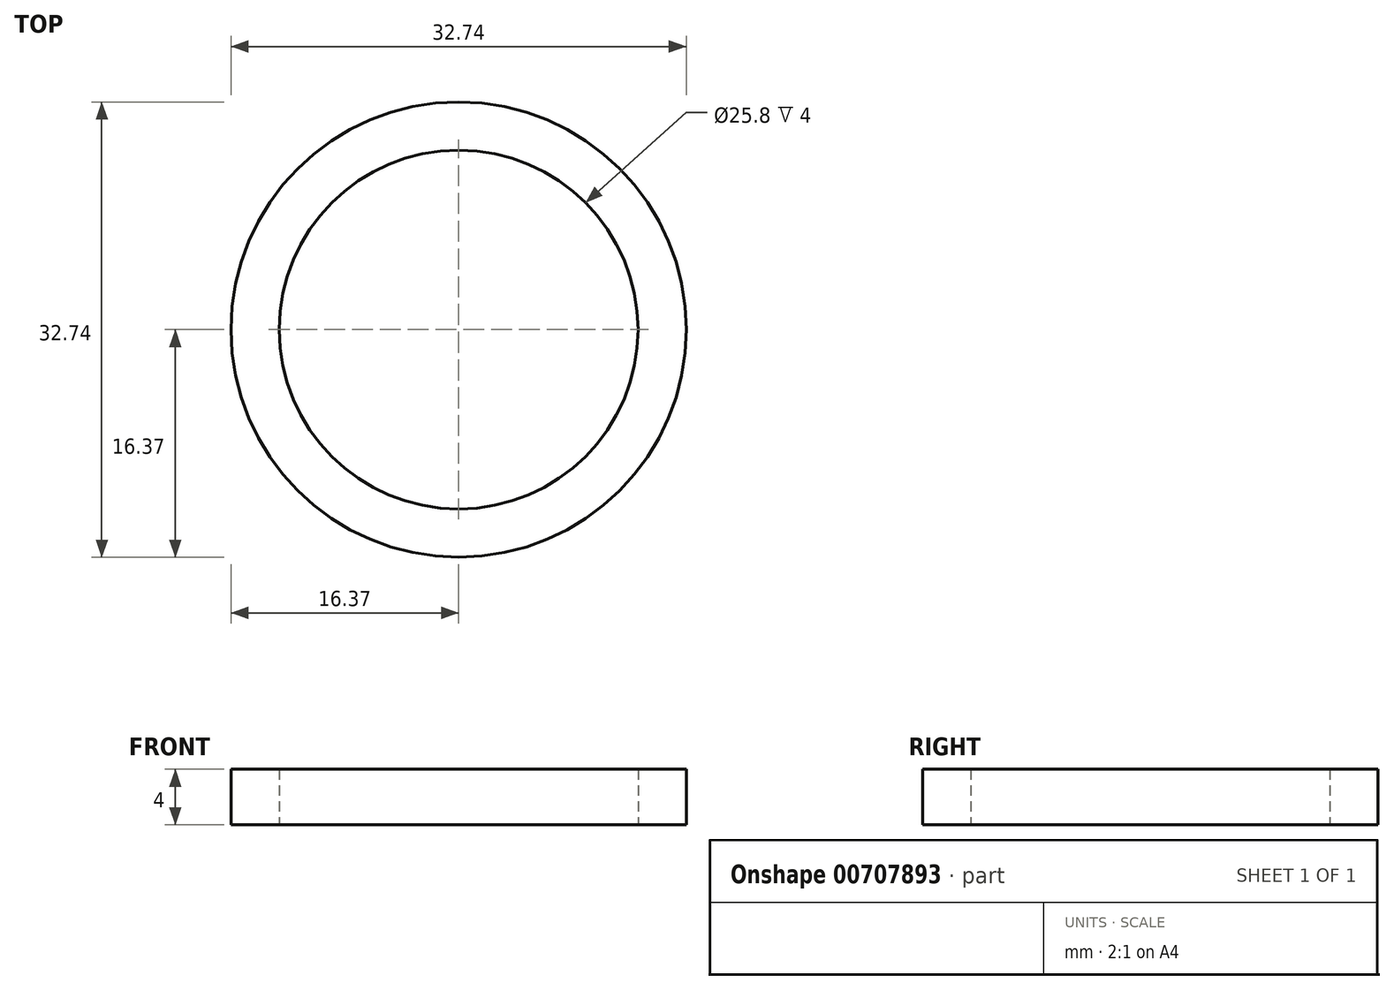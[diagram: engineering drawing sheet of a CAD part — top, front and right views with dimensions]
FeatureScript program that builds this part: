
annotation { "Feature Type Name" : "Feature", "Feature Type Description" : "" }
export const myFeature = defineFeature(function(context is Context, id is Id, definition is map)
    precondition{}
    {
        {
            var Q0;
            Q0=qCreatedBy(makeId("Top.planeOp"),FACE);
            var sketch = newSketch(context, id + "F0", { "sketchPlane" : qUnion([Q0])});
            skCircle(sketch, "E0", {"center": v(0, 0) * mm, "radius": 12.9 * mm});
            skCircle(sketch, "E1", {"center": v(0, 0) * mm, "radius": 16.37 * mm});
            skSolve(sketch);
        }
        {
            var Q0;
            Q0=makeQuery(id+"F0.imprint","IMPRINT",FACE,{"disambiguationData":[TD([[makeQuery(id+"F0.imprint","IMPRINT",EDGE,{"derivedFrom":sQuery(id+"F0.wireOp",EDGE,"E0")}),-1.0]])]});
            extrude(context, id + "F1", {"entities" : qUnion([Q0]), "depth" : 4 * mm, "offsetDistance" : 25 * mm});
        }
    });
